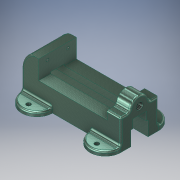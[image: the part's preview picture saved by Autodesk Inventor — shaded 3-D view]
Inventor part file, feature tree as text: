
AUTODESK INVENTOR PART (.ipt)
format: ipt  version: 2017 (Build 210142000, 142)  size: 376,832 bytes
history: native  units: in
note: dims shown in document units (in); Inventor stores cm internally (conversion verified against a paired STEP export)
features: extrude x4, sketch x4, hole x3, plane x2, mirror x2, fillet x2
ambient origin geometry x8: Origin, YZ Plane, XZ Plane, XY Plane, X Axis, Y Axis, Z Axis, Center Point
bodies: Solid1 (feature_tree)
feature tree (17):
  extrude  "Extrusion1"  Depth=2.1875in
  extrude  "Extrusion2"  Depth=0.625in
  plane  "Work Plane2"
  mirror  "Mirror1"
  plane  "Work Plane3"
  mirror  "Mirror3"
  extrude  "Extrusion3"  Depth=1.1875in
  extrude  "Extrusion4"  Depth=0.625in
  fillet  "1/4R Fillet"  Radius=2.75in
  fillet  "1/8R Fillet"  Radius=1.125in
  hole  "5/8-8ACME"  [1 undecoded]
  hole  "(1) 1/4-20UNC-2B"  [1 undecoded]
  hole  "(2) 1/4-20UNC-2B"  [1 undecoded]
  sketch  "Sketch1"  dims[d0=7.25in d1=2.1875in]
  sketch  "Sketch2"  dims[d4=1.0in d5=0.625in]
  sketch  "Sketch3"  dims[d6=5.0in d7=1.1875in]
  sketch  "Sketch4"  dims[d8=1.375in d9=2.9375in d10=2.75in d11=0.0in d12=1.125in d14=0.3125in d16=2.25in d17=0.625in d18=1.125in d23=0.3125in d24=0.0in d26=-1.375in d27=-3.625in d28=2.25in d29=1.375in d30=1.375in d31=1.0in d32=0.0in d33=1.375in d34=0.501in d35=0.626in d36=1.002in d37=1.252in d38=1.0625in d39=1.6875in d40=3.5in d41=1.0in d42=0.0in d43=0.25in d44=0.125in d63=1.0in d64=1.0in d47=0.5in d48=1.0in d49=0.119in d50=0.25in d51=0.5635in d52=0.146in d53=0.0in d54=1.0in d55=0.625in d56=0.196in d57=0.5in d58=0.119in d59=0.25in d60=0.5635in d61=0.625in d62=0.0in d65=2.125in d66=1.0in d67=0.196in d68=0.625in d69=0.119in d70=0.25in d71=0.5635in d72=0.625in d73=0.0in]
note: 3 required parameter values undecoded (feature->parameter linkage not recoverable at this tier; creation-order binding heuristic only, values carry confidence <= 0.55)
